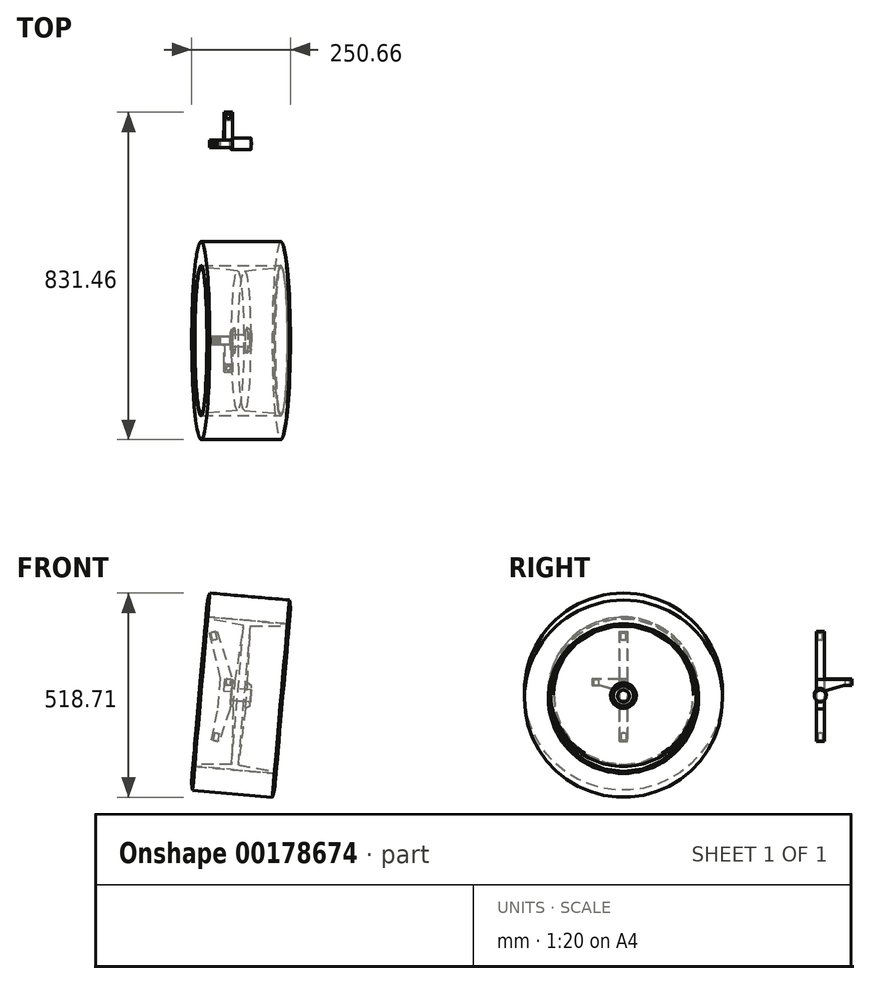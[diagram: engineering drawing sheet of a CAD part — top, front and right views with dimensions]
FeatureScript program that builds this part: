
annotation { "Feature Type Name" : "Feature", "Feature Type Description" : "" }
export const myFeature = defineFeature(function(context is Context, id is Id, definition is map)
    precondition{}
    {
        {
            var Q0;
            Q0=qCreatedBy(makeId("Front.planeOp"),FACE);
            var sketch = newSketch(context, id + "F0", { "sketchPlane" : qUnion([Q0])});
            skLineSegment(sketch, "E0", {"start": v(0, 195.2) * mm, "end": v(0, -200.25) * mm, "construction": true});
            skLineSegment(sketch, "E1", {"start": v(22.1, 171.93) * mm, "end": v(61.54, 49) * mm});
            skLineSegment(sketch, "E2", {"start": v(61.54, 49) * mm, "end": v(55, -25.72) * mm});
            skLineSegment(sketch, "E3", {"start": v(55, -25.72) * mm, "end": v(27.69, -108.53) * mm});
            skLineSegment(sketch, "E4", {"start": v(27.69, -108.53) * mm, "end": v(8.1, -104.44) * mm});
            skLineSegment(sketch, "E5", {"start": v(8.1, -104.44) * mm, "end": v(25.12, -23.1) * mm});
            skLineSegment(sketch, "E6", {"start": v(25.12, -23.1) * mm, "end": v(31.66, 51.6) * mm});
            skLineSegment(sketch, "E7", {"start": v(31.66, 51.6) * mm, "end": v(2.7, 167.07) * mm});
            skLineSegment(sketch, "E8", {"start": v(2.7, 167.07) * mm, "end": v(22.1, 171.93) * mm});
            skLineSegment(sketch, "E9", {"start": v(77.72, 233.86) * mm, "end": v(1.17, -641.1) * mm, "construction": true});
            skLineSegment(sketch, "E10", {"start": v(61.54, 49) * mm, "end": v(-208.12, 72.58) * mm, "construction": true});
            skLineSegment(sketch, "E11", {"start": v(55, -25.72) * mm, "end": v(-212.03, -2.36) * mm, "construction": true});
            skLineSegment(sketch, "E12", {"start": v(141.06, 4.4) * mm, "end": v(-205.15, 34.68) * mm, "construction": true});
            skSolve(sketch);
        }
        {
            var Q0;
            Q0 = qSketchRegion(id + "F0", true);
            extrude(context, id + "F1", {"entities" : qUnion([Q0]), "endBound" : BoundingType.SYMMETRIC, "depth" : 20 * mm});
        }
        {
            var Q0;
            Q0=makeQuery(id+"F1.opExtrude","SWEPT_FACE",FACE,{"disambiguationData":[OSD([sQuery(id+"F0.wireOp",EDGE,"E2")])]});
            var sketch = newSketch(context, id + "F2", { "sketchPlane" : qUnion([Q0])});
            skCircle(sketch, "E13", {"center": v(0, 16.67) * mm, "radius": 15 * mm});
            skLineSegment(sketch, "E14", {"start": v(-21.08, 16.67) * mm, "end": v(59.96, 16.67) * mm, "construction": true});
            skPoint(sketch, "E14.startSnap0", {"position": v(-10, 16.67) * mm});
            skSolve(sketch);
        }
        {
            var Q0;
            Q0 = qSketchRegion(id + "F2", true);
            extrude(context, id + "F3", {"entities" : qUnion([Q0]), "operationType" : NewBodyOperationType.ADD, "depth" : 50 * mm});
        }
        {
            var Q0;
            Q0=makeQuery(id+"F1.opExtrude","SWEPT_BODY",BODY,{"disambiguationData":[OSD([sQuery(id+"F0.wireOp",EDGE,"E1"),sQuery(id+"F0.wireOp",EDGE,"E2"),sQuery(id+"F0.wireOp",EDGE,"E3"),sQuery(id+"F0.wireOp",EDGE,"E4"),sQuery(id+"F0.wireOp",EDGE,"E5"),sQuery(id+"F0.wireOp",EDGE,"E6"),sQuery(id+"F0.wireOp",EDGE,"E7"),sQuery(id+"F0.wireOp",EDGE,"E8")])]});
            transform(context, id + "F4", {"entities" : qUnion([Q0]), "transformType" : TransformType.TRANSLATION_3D, "dx" : 0 * mm, "dy" : 500 * mm, "dz" : 0 * mm, "makeCopy" : true});
        }
        {
            var Q0;
            Q0=makeQuery(id+"F1.opExtrude","SWEPT_FACE",FACE,{"disambiguationData":[OSD([sQuery(id+"F0.wireOp",EDGE,"E2")])]});
            var sketch = newSketch(context, id + "F5", { "sketchPlane" : qUnion([Q0])});
            skLineSegment(sketch, "E15", {"start": v(-10, 54.17) * mm, "end": v(-80, 54.17) * mm});
            skLineSegment(sketch, "E16", {"start": v(-80, 54.17) * mm, "end": v(-80, 39.17) * mm});
            skLineSegment(sketch, "E17", {"start": v(-80, 39.17) * mm, "end": v(-60, 39.17) * mm});
            skLineSegment(sketch, "E18", {"start": v(-60, 39.17) * mm, "end": v(-10, 24.17) * mm});
            skLineSegment(sketch, "E19", {"start": v(-10, 54.17) * mm, "end": v(-10, 24.17) * mm});
            skSolve(sketch);
        }
        {
            var Q0;
            {var subQ1=sQuery(id+"F5.wireOp",EDGE,"E15");Q0=makeQuery(id+"F5.imprint","IMPRINT",FACE,{"disambiguationData":[TD([[makeQuery(id+"F5.imprint","IMPRINT",EDGE,{"derivedFrom":subQ1}),1.0]])]});}
            extrude(context, id + "F6", {"entities" : qUnion([Q0]), "operationType" : NewBodyOperationType.ADD, "oppositeDirection" : true, "depth" : 20 * mm});
        }
        {
            var Q0;
            Q0=makeQuery(id+"F6.opExtrude","SWEPT_FACE",FACE,{"disambiguationData":[OSD([sQuery(id+"F5.wireOp",EDGE,"E17")])]});
            var sketch = newSketch(context, id + "F7", { "sketchPlane" : qUnion([Q0])});
            skLineSegment(sketch, "E20", {"start": v(47.04, 54.98) * mm, "end": v(47.04, 93.52) * mm, "construction": true});
            skPoint(sketch, "E20.startSnap0", {"position": v(47.04, 60) * mm});
            skPoint(sketch, "E20.endSnap0", {"position": v(47.04, 80) * mm});
            skLineSegment(sketch, "E21", {"start": v(30.33, 70) * mm, "end": v(69.98, 70) * mm, "construction": true});
            skPoint(sketch, "E21.startSnap0", {"position": v(37.04, 70) * mm});
            skCircle(sketch, "E22", {"center": v(47.04, 70) * mm, "radius": 6 * mm});
            skSolve(sketch);
        }
        {
            var Q0;
            Q0 = qSketchRegion(id + "F7", true);
            extrude(context, id + "F8", {"entities" : qUnion([Q0]), "operationType" : NewBodyOperationType.REMOVE, "endBound" : BoundingType.THROUGH_ALL, "oppositeDirection" : true, "depth" : 25 * mm});
        }
        {
            var Q0;
            Q0=makeQuery(id+"F1.opExtrude","SWEPT_FACE",FACE,{"disambiguationData":[OSD([sQuery(id+"F0.wireOp",EDGE,"E8")])]});
            var sketch = newSketch(context, id + "F9", { "sketchPlane" : qUnion([Q0])});
            skLineSegment(sketch, "E23", {"start": v(23.73, 0) * mm, "end": v(-73.3, 0) * mm, "construction": true});
            skPoint(sketch, "E23.endSnap0", {"position": v(63.26, 0) * mm});
            skLineSegment(sketch, "E24", {"start": v(53.26, -38.65) * mm, "end": v(53.26, 35.78) * mm, "construction": true});
            skPoint(sketch, "E24.startSnap0", {"position": v(53.26, -10) * mm});
            skCircle(sketch, "E25", {"center": v(53.26, 0) * mm, "radius": 6 * mm});
            skSolve(sketch);
        }
        {
            var Q0;
            Q0 = qSketchRegion(id + "F9", true);
            extrude(context, id + "F10", {"entities" : qUnion([Q0]), "operationType" : NewBodyOperationType.REMOVE, "oppositeDirection" : true, "depth" : 20 * mm});
        }
        {
            var Q0;
            Q0=makeQuery(id+"F1.opExtrude","SWEPT_FACE",FACE,{"disambiguationData":[OSD([sQuery(id+"F0.wireOp",EDGE,"E4")])]});
            var sketch = newSketch(context, id + "F11", { "sketchPlane" : qUnion([Q0])});
            skLineSegment(sketch, "E26", {"start": v(-17, 0) * mm, "end": v(100.49, 0) * mm, "construction": true});
            skLineSegment(sketch, "E27", {"start": v(39.32, -28.2) * mm, "end": v(39.32, 57.2) * mm, "construction": true});
            skPoint(sketch, "E27.startSnap0", {"position": v(39.32, -10) * mm});
            skCircle(sketch, "E28", {"center": v(39.32, 0) * mm, "radius": 6 * mm});
            skSolve(sketch);
        }
        {
            var Q0;
            Q0 = qSketchRegion(id + "F11", true);
            extrude(context, id + "F12", {"entities" : qUnion([Q0]), "operationType" : NewBodyOperationType.REMOVE, "oppositeDirection" : true, "depth" : 20 * mm});
        }
        {
            var Q0;
            Q0=qCreatedBy(makeId("Front.planeOp"),FACE);
            var sketch = newSketch(context, id + "F13", { "sketchPlane" : qUnion([Q0])});
            skLineSegment(sketch, "E29", {"start": v(59.58, 26.58) * mm, "end": v(110.33, 22.14) * mm, "construction": true});
            skLineSegment(sketch, "E30.0", {"start": v(109.4, 22.22) * mm, "end": v(106.78, -7.67) * mm, "construction": true});
            skLineSegment(sketch, "E31", {"start": v(240.38, -4.3) * mm, "end": v(-99.22, 25.41) * mm, "construction": true});
            skLineSegment(sketch, "E32", {"start": v(59.58, 26.58) * mm, "end": v(60.52, 37.3) * mm});
            skLineSegment(sketch, "E33", {"start": v(110.33, 32.94) * mm, "end": v(109.4, 22.22) * mm});
            skLineSegment(sketch, "E34", {"start": v(-35.82, 211.1) * mm, "end": v(269.76, 184.36) * mm, "construction": true});
            skLineSegment(sketch, "E35", {"start": v(-1.43, 208.08) * mm, "end": v(201, 190.37) * mm});
            skLineSegment(sketch, "E36", {"start": v(-1.43, 208.08) * mm, "end": v(-1.87, 203.1) * mm});
            skLineSegment(sketch, "E37", {"start": v(-1.87, 203.1) * mm, "end": v(89.96, 186.91) * mm});
            skLineSegment(sketch, "E38", {"start": v(89.96, 186.91) * mm, "end": v(68.54, 43.85) * mm});
            skLineSegment(sketch, "E39", {"start": v(68.54, 43.85) * mm, "end": v(60.52, 37.3) * mm});
            skLineSegment(sketch, "E40", {"start": v(201, 190.37) * mm, "end": v(200.56, 185.4) * mm});
            skLineSegment(sketch, "E41", {"start": v(200.56, 185.4) * mm, "end": v(107.32, 185.4) * mm});
            skLineSegment(sketch, "E42", {"start": v(107.32, 185.4) * mm, "end": v(100.16, 40.92) * mm});
            skLineSegment(sketch, "E43", {"start": v(100.16, 40.92) * mm, "end": v(110.33, 32.94) * mm});
            skLineSegment(sketch, "E44", {"start": v(59.58, 26.58) * mm, "end": v(110.33, 22.14) * mm});
            skLineSegment(sketch, "E45", {"start": v(106.78, -7.67) * mm, "end": v(56.97, -3.3) * mm, "construction": true});
            skLineSegment(sketch, "E46", {"start": v(77.43, -56.23) * mm, "end": v(106.55, 276.61) * mm, "construction": true});
            skSolve(sketch);
        }
        {
            var Q0;
            Q0 = qSketchRegion(id + "F13", true);
            var Q1;
            Q1=makeQuery(id+"F3.opExtrude","SWEPT_FACE",FACE,{"disambiguationData":[OSD([sQuery(id+"F2.wireOp",EDGE,"E13")])]});
            revolve(context, id + "F14", {"entities" : qUnion([Q0]), "axis" : qUnion([Q1]), "revolveType" : RevolveType.FULL});
        }
        {
            var Q0;
            Q0=qCreatedBy(makeId("Front.planeOp"),FACE);
            var sketch = newSketch(context, id + "F15", { "sketchPlane" : qUnion([Q0])});
            skLineSegment(sketch, "E47", {"start": v(-1.43, 208.08) * mm, "end": v(201, 190.37) * mm, "construction": true});
            skLineSegment(sketch, "E48.0", {"start": v(-1.43, 208.08) * mm, "end": v(-34.64, -171.47) * mm, "construction": true});
            skLineSegment(sketch, "E49.0", {"start": v(201, 190.37) * mm, "end": v(167.79, -189.18) * mm, "construction": true});
            skLineSegment(sketch, "E50", {"start": v(3.88, 268.81) * mm, "end": v(206.3, 251.1) * mm});
            skLineSegment(sketch, "E51", {"start": v(116.7, 392.7) * mm, "end": v(90.07, 88.2) * mm, "construction": true});
            skLineSegment(sketch, "E52", {"start": v(21.36, 236.69) * mm, "end": v(295, 212.75) * mm, "construction": true});
            skArc(sketch, "E53", {"start": v(3.88, 268.81) * mm, "mid": v(-3.23, 238.84) * mm, "end": v(-1.43, 208.08) * mm});
            skArc(sketch, "E54", {"start": v(206.3, 251.1) * mm, "mid": v(208.1, 220.35) * mm, "end": v(201, 190.37) * mm});
            skLineSegment(sketch, "E55", {"start": v(-1.43, 208.08) * mm, "end": v(201, 190.37) * mm});
            skSolve(sketch);
        }
        {
            var Q0;
            Q0 = qSketchRegion(id + "F15", true);
            var Q1;
            Q1=makeQuery(id+"F14.opRevolve","SWEPT_FACE",FACE,{"disambiguationData":[OSD([sQuery(id+"F13.wireOp",EDGE,"E35")])]});
            revolve(context, id + "F16", {"entities" : qUnion([Q0]), "axis" : qUnion([Q1]), "revolveType" : RevolveType.FULL});
        }
        {
            var Q0;
            {var subQ6=sQuery(id+"F0.wireOp",EDGE,"E2");var subQ7=sQuery(id+"F0.wireOp",EDGE,"E1");Q0=makeQuery(id+"F4.opPattern","COPY",FACE,{"derivedFrom":makeQuery(id+"F3.boolean.opBoolean","SPLIT",FACE,{"disambiguationData":[TD([makeQuery(id+"F1.opExtrude","SWEPT_FACE",FACE,{"disambiguationData":[OSD([subQ7])]})])],"derivedFrom":makeQuery(id+"F1.opExtrude","SWEPT_FACE",FACE,{"disambiguationData":[OSD([subQ6])]})}),"instanceName":"1"});}
            var sketch = newSketch(context, id + "F17", { "sketchPlane" : qUnion([Q0])});
            skLineSegment(sketch, "E56", {"start": v(510, 54.17) * mm, "end": v(580, 54.17) * mm});
            skLineSegment(sketch, "E57", {"start": v(580, 54.17) * mm, "end": v(580, 39.17) * mm});
            skLineSegment(sketch, "E58", {"start": v(580, 39.17) * mm, "end": v(560, 39.17) * mm});
            skLineSegment(sketch, "E59", {"start": v(560, 39.17) * mm, "end": v(510, 24.17) * mm});
            skLineSegment(sketch, "E60", {"start": v(510, 24.17) * mm, "end": v(510, 54.17) * mm});
            skSolve(sketch);
        }
        {
            var Q0;
            Q0 = qSketchRegion(id + "F17", true);
            extrude(context, id + "F18", {"entities" : qUnion([Q0]), "operationType" : NewBodyOperationType.ADD, "oppositeDirection" : true, "depth" : 20 * mm});
        }
        {
            var Q0;
            Q0=makeQuery(id+"F18.opExtrude","SWEPT_FACE",FACE,{"disambiguationData":[OSD([sQuery(id+"F17.wireOp",EDGE,"E56")])]});
            var sketch = newSketch(context, id + "F19", { "sketchPlane" : qUnion([Q0])});
            skCircle(sketch, "E61", {"center": v(47.04, 570) * mm, "radius": 6 * mm});
            skSolve(sketch);
        }
        {
            var Q0;
            Q0 = qSketchRegion(id + "F19", true);
            extrude(context, id + "F20", {"entities" : qUnion([Q0]), "operationType" : NewBodyOperationType.REMOVE, "endBound" : BoundingType.THROUGH_ALL, "oppositeDirection" : true, "depth" : 25 * mm});
        }
        {
            var Q0;
            Q0=makeQuery(id+"F4.opPattern","COPY",FACE,{"derivedFrom":makeQuery(id+"F1.opExtrude","SWEPT_FACE",FACE,{"disambiguationData":[OSD([sQuery(id+"F0.wireOp",EDGE,"E8")])]}),"instanceName":"1"});
            var sketch = newSketch(context, id + "F21", { "sketchPlane" : qUnion([Q0])});
            skCircle(sketch, "E62", {"center": v(53.26, 500) * mm, "radius": 6 * mm});
            skPoint(sketch, "E62.centerSnap0", {"position": v(53.26, 510) * mm});
            skPoint(sketch, "E62.centerSnap1", {"position": v(43.26, 500) * mm});
            skSolve(sketch);
        }
        {
            var Q0;
            Q0 = qSketchRegion(id + "F21", true);
            extrude(context, id + "F22", {"entities" : qUnion([Q0]), "operationType" : NewBodyOperationType.REMOVE, "oppositeDirection" : true, "depth" : 20 * mm});
        }
        {
            var Q0;
            Q0=makeQuery(id+"F4.opPattern","COPY",FACE,{"derivedFrom":makeQuery(id+"F1.opExtrude","SWEPT_FACE",FACE,{"disambiguationData":[OSD([sQuery(id+"F0.wireOp",EDGE,"E4")])]}),"instanceName":"1"});
            var sketch = newSketch(context, id + "F23", { "sketchPlane" : qUnion([Q0])});
            skCircle(sketch, "E63", {"center": v(39.32, -500) * mm, "radius": 6 * mm});
            skPoint(sketch, "E63.centerSnap0", {"position": v(39.32, -510) * mm});
            skPoint(sketch, "E63.centerSnap1", {"position": v(29.32, -500) * mm});
            skSolve(sketch);
        }
        {
            var Q0;
            Q0 = qSketchRegion(id + "F23", true);
            extrude(context, id + "F24", {"entities" : qUnion([Q0]), "operationType" : NewBodyOperationType.REMOVE, "oppositeDirection" : true, "depth" : 20 * mm});
        }
    });
